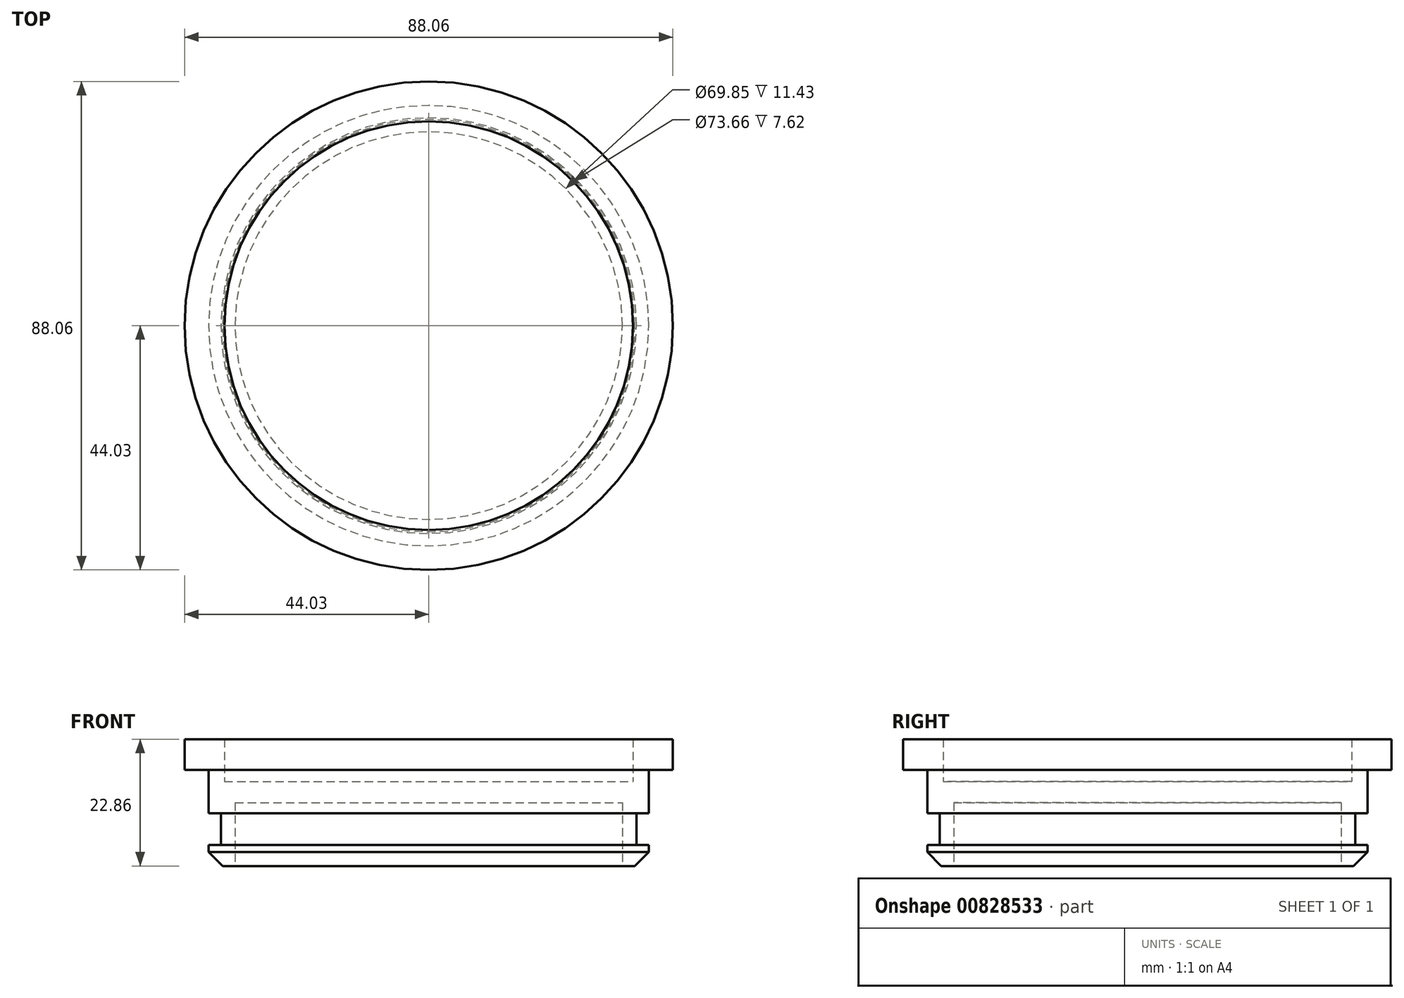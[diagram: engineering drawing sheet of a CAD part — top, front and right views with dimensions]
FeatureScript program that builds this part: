
annotation { "Feature Type Name" : "Feature", "Feature Type Description" : "" }
export const myFeature = defineFeature(function(context is Context, id is Id, definition is map)
    precondition{}
    {
        {
            var Q0;
            Q0=qCreatedBy(makeId("Front.planeOp"),FACE);
            var sketch = newSketch(context, id + "F0", { "sketchPlane" : qUnion([Q0])});
            skLineSegment(sketch, "E0", {"start": v(0, -7.62) * mm, "end": v(0, 0) * mm, "construction": true});
            skLineSegment(sketch, "E1", {"start": v(0, -7.62) * mm, "end": v(36.83, -7.62) * mm});
            skLineSegment(sketch, "E2", {"start": v(36.83, -7.62) * mm, "end": v(36.83, 0) * mm});
            skLineSegment(sketch, "E3", {"start": v(36.83, 0) * mm, "end": v(44.03, 0) * mm});
            skLineSegment(sketch, "E4", {"start": v(44.03, 0) * mm, "end": v(44.03, -5.56) * mm});
            skLineSegment(sketch, "E5", {"start": v(44.03, -5.56) * mm, "end": v(39.69, -5.56) * mm});
            skLineSegment(sketch, "E6", {"start": v(39.69, -5.56) * mm, "end": v(39.69, -13.33) * mm});
            skLineSegment(sketch, "E7", {"start": v(39.69, -13.33) * mm, "end": v(37.47, -13.33) * mm});
            skLineSegment(sketch, "E8", {"start": v(37.47, -13.33) * mm, "end": v(37.47, -19.05) * mm});
            skLineSegment(sketch, "E9", {"start": v(37.47, -19.05) * mm, "end": v(39.69, -19.05) * mm});
            skLineSegment(sketch, "E10", {"start": v(39.69, -19.05) * mm, "end": v(39.69, -20.35) * mm});
            skLineSegment(sketch, "E11", {"start": v(39.69, -20.35) * mm, "end": v(37.17, -22.86) * mm});
            skLineSegment(sketch, "E12", {"start": v(37.17, -22.86) * mm, "end": v(34.93, -22.86) * mm});
            skLineSegment(sketch, "E13", {"start": v(0, -11.43) * mm, "end": v(0, -7.62) * mm});
            skLineSegment(sketch, "E14", {"start": v(34.93, -22.86) * mm, "end": v(34.93, -11.43) * mm});
            skLineSegment(sketch, "E15", {"start": v(34.93, -11.43) * mm, "end": v(0, -11.43) * mm});
            skSolve(sketch);
        }
        {
            var Q0;
            Q0 = qSketchRegion(id + "F0", true);
            var Q1;
            Q1=sQuery(id+"F0.wireOp",EDGE,"E0");
            revolve(context, id + "F1", {"surfaceOperationType" : NewSurfaceOperationType.NEW, "entities" : qUnion([Q0]), "axis" : qUnion([Q1]), "revolveType" : RevolveType.FULL});
        }
    });
